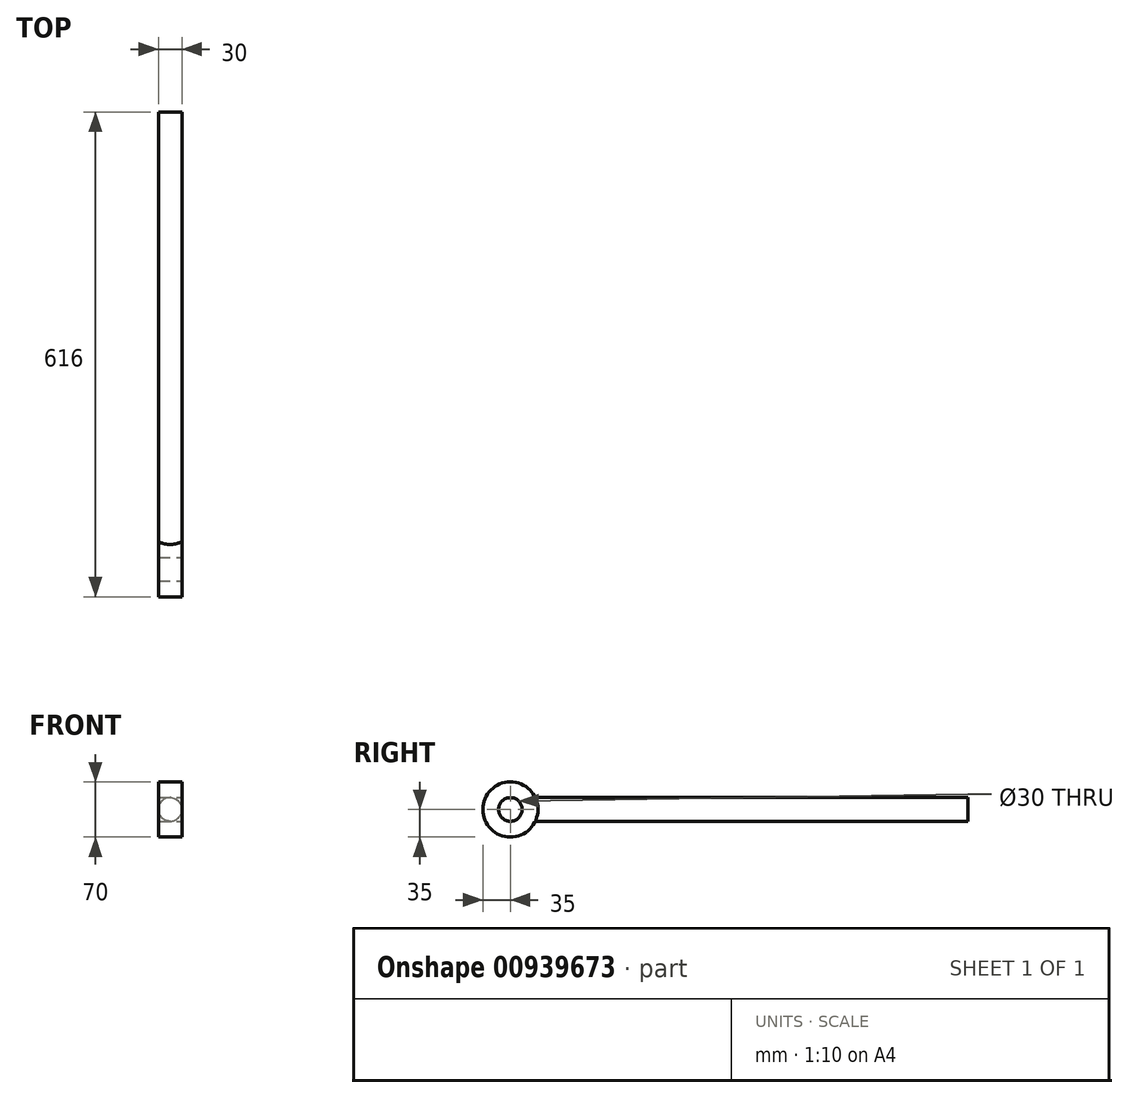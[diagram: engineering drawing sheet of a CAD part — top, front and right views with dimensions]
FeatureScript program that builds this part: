
annotation { "Feature Type Name" : "Feature", "Feature Type Description" : "" }
export const myFeature = defineFeature(function(context is Context, id is Id, definition is map)
    precondition{}
    {
        {
            var Q0;
            Q0=qCreatedBy(makeId("Front.planeOp"),FACE);
            var sketch = newSketch(context, id + "F0", { "sketchPlane" : qUnion([Q0])});
            skCircle(sketch, "E0", {"center": v(0, 0) * mm, "radius": 15 * mm});
            skSolve(sketch);
        }
        {
            var Q0;
            Q0 = qSketchRegion(id + "F0", true);
            extrude(context, id + "F1", {"entities" : qUnion([Q0]), "oppositeDirection" : true, "depth" : 550 * mm, "offsetDistance" : 25 * mm});
        }
        {
            var Q0;
            Q0=qCreatedBy(makeId("Right.planeOp"),FACE);
            var sketch = newSketch(context, id + "F2", { "sketchPlane" : qUnion([Q0])});
            skCircle(sketch, "E1", {"center": v(-31, 0) * mm, "radius": 35 * mm});
            skSolve(sketch);
        }
        {
            var Q0;
            Q0 = qSketchRegion(id + "F2", true);
            extrude(context, id + "F3", {"entities" : qUnion([Q0]), "operationType" : NewBodyOperationType.ADD, "depth" : 15 * mm, "offsetDistance" : 25 * mm, "hasSecondDirection" : true, "secondDirectionOppositeDirection" : true, "secondDirectionDepth" : 15 * mm});
        }
        {
            var Q0;
            Q0=makeQuery(id+"F3.opExtrude","CAP_FACE",FACE,{"disambiguationData":[OSD([sQuery(id+"F2.wireOp",EDGE,"E1")])],"isStart":false});
            var sketch = newSketch(context, id + "F4", { "sketchPlane" : qUnion([Q0])});
            skCircle(sketch, "E2", {"center": v(-31, 0) * mm, "radius": 15 * mm});
            skSolve(sketch);
        }
        {
            var Q0;
            Q0 = qSketchRegion(id + "F4", true);
            extrude(context, id + "F5", {"entities" : qUnion([Q0]), "operationType" : NewBodyOperationType.REMOVE, "endBound" : BoundingType.THROUGH_ALL, "oppositeDirection" : true, "depth" : 25 * mm, "offsetDistance" : 25 * mm});
        }
    });
